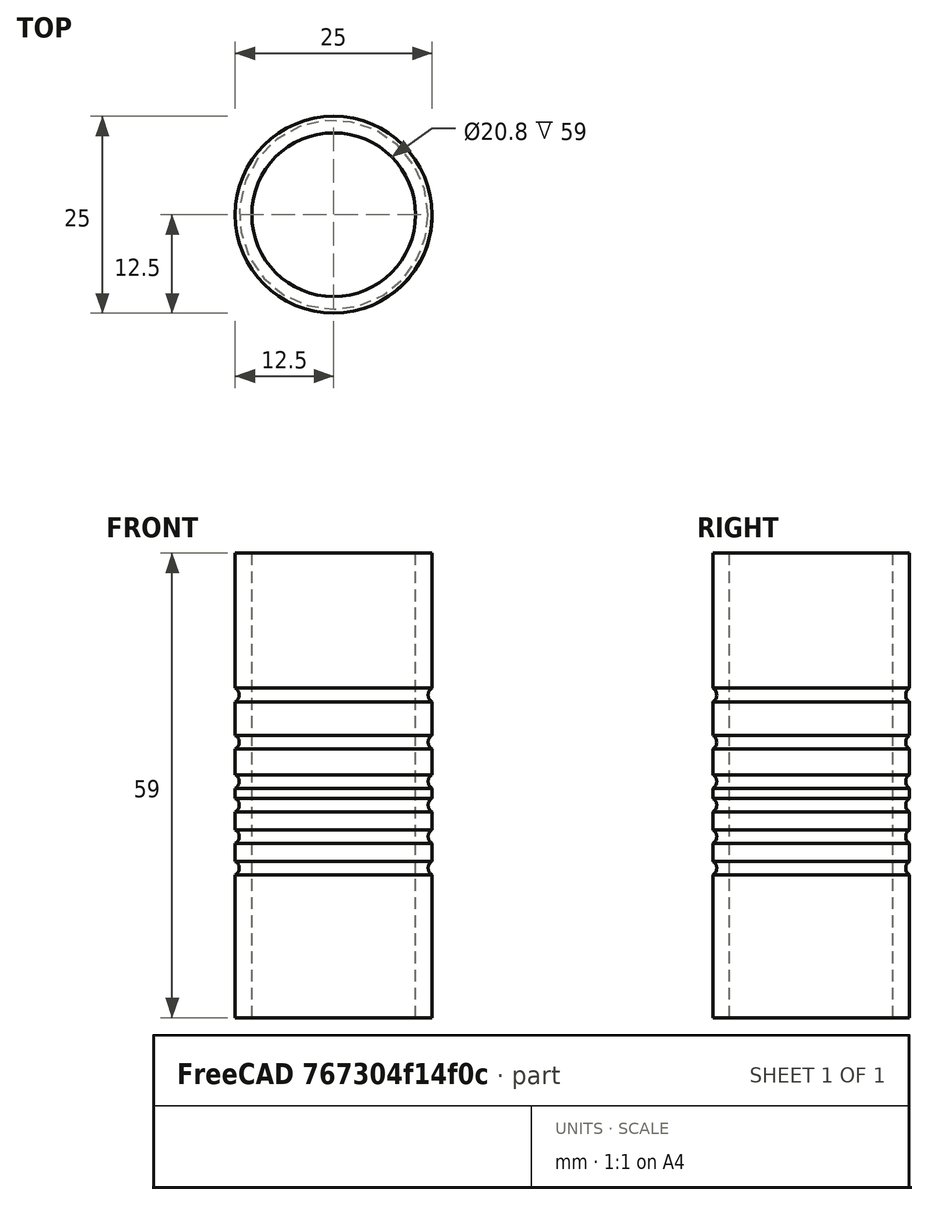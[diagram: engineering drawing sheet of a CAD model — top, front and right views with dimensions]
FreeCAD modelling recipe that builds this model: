
FCSTD DOCUMENT
Label: Part6
License: CC-BY 3.0
LicenseURL: http://creativecommons.org/licenses/by/3.0/
objects: Part::Cut×7, Part::Torus×6, Part::Cylinder×2
note: 15 computed .brp shape members not serialized (recipe doc carries the construction recipe); baked Part::Feature solids carry a one-line shape summary decoded from their .brp

FEATURE [Part::Cylinder] Cylinder
  Angle = 360
  Height = 59
  Radius = 12.5
FEATURE [Part::Cylinder] Cylinder001
  Angle = 360
  Height = 59
  Radius = 10.4
FEATURE [Part::Torus] Torus
  Angle1 = -180
  Angle2 = 180
  Angle3 = 360
  Placement = pos=(0,0,35) rot=(0,0,1;0rad)
  Radius1 = 13
  Radius2 = 1
FEATURE [Part::Torus] Torus001
  Angle1 = -180
  Angle2 = 180
  Angle3 = 360
  Placement = pos=(0,0,30) rot=(0,0,1;0rad)
  Radius1 = 13
  Radius2 = 1
FEATURE [Part::Torus] Torus001001
  Angle1 = -180
  Angle2 = 180
  Angle3 = 360
  Placement = pos=(0,0,27) rot=(0,0,1;0rad)
  Radius1 = 13
  Radius2 = 1
FEATURE [Part::Torus] Torus001002
  Angle1 = -180
  Angle2 = 180
  Angle3 = 360
  Placement = pos=(0,0,23) rot=(0,0,1;0rad)
  Radius1 = 13
  Radius2 = 1
FEATURE [Part::Torus] Torus001002001
  Angle1 = -180
  Angle2 = 180
  Angle3 = 360
  Placement = pos=(0,0,19) rot=(0,0,1;0rad)
  Radius1 = 13
  Radius2 = 1
FEATURE [Part::Cut] Cut
  Base = -> Cylinder
  Tool = -> Cylinder001
FEATURE [Part::Torus] Torus001002002
  Angle1 = -180
  Angle2 = 180
  Angle3 = 360
  Placement = pos=(0,0,41) rot=(0,0,1;0rad)
  Radius1 = 13
  Radius2 = 1
FEATURE [Part::Cut] Cut001
  Base = -> Cut
  Tool = -> Torus001002002
FEATURE [Part::Cut] Cut002
  Base = -> Cut001
  Tool = -> Torus
FEATURE [Part::Cut] Cut003
  Base = -> Cut002
  Tool = -> Torus001
FEATURE [Part::Cut] Cut004
  Base = -> Cut003
  Tool = -> Torus001001
FEATURE [Part::Cut] Cut005
  Base = -> Cut004
  Tool = -> Torus001002
FEATURE [Part::Cut] Cut006
  Base = -> Cut005
  Tool = -> Torus001002001
